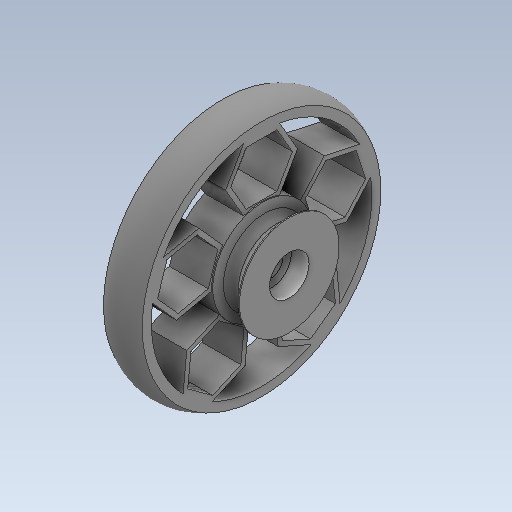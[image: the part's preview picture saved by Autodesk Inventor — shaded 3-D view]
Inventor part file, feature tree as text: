
AUTODESK INVENTOR PART (.ipt)
format: ipt  version: 2020 (Build 240168000, 168)  size: 318,464 bytes
history: native  units: in
note: dims shown in document units (in); Inventor stores cm internally (conversion verified against a paired STEP export)
features: sketch x4, other x3, extrude x3, revolve x1, projected_geometry x1
ambient origin geometry x8: Origin, YZ Plane, XZ Plane, XY Plane, X Axis, Y Axis, Z Axis, Center Point
bodies: Solid1 (feature_tree)
feature tree (12):
  other  "PulleyedWheelV1.ipt"
  extrude  "Extrusion1"  Depth=0.2756in
  extrude  "Extrusion2"  Depth=0.126in
  extrude  "Extrusion3"  Depth=0.126in
  revolve  "Revolution1"  [1 undecoded]
  other  "Solid1::PulleyedWheelV1.ipt"
  other  "TaggingFeature1"
  sketch  "Sketch1"  dims[d0=0.3937in]
  sketch  "Sketch2"  dims[d1=0.0394in d3=1.6929in d4=0.1181in d6=0.7087in d7=0.1969in d8=0.0in d9=1.6929in d10=0.063in d11=0.0315in d16=0.2756in d17=0.0in d20=0.0984in d24=0.0394in d26=45.0deg d2=0.2815in]
  sketch  "Sketch3"  dims[d5=0.126in d13=0.0in d15=0.2815in]
  sketch  "Sketch4"  dims[d18=0.126in d19=0.0in d21=0.1575in d23=0.0in d25=0.0in d28=45.0deg d29=90.0deg]
  projected_geometry  "Projected Loop1"
note: 1 required parameter value undecoded (feature->parameter linkage not recoverable at this tier; creation-order binding heuristic only, values carry confidence <= 0.55)
